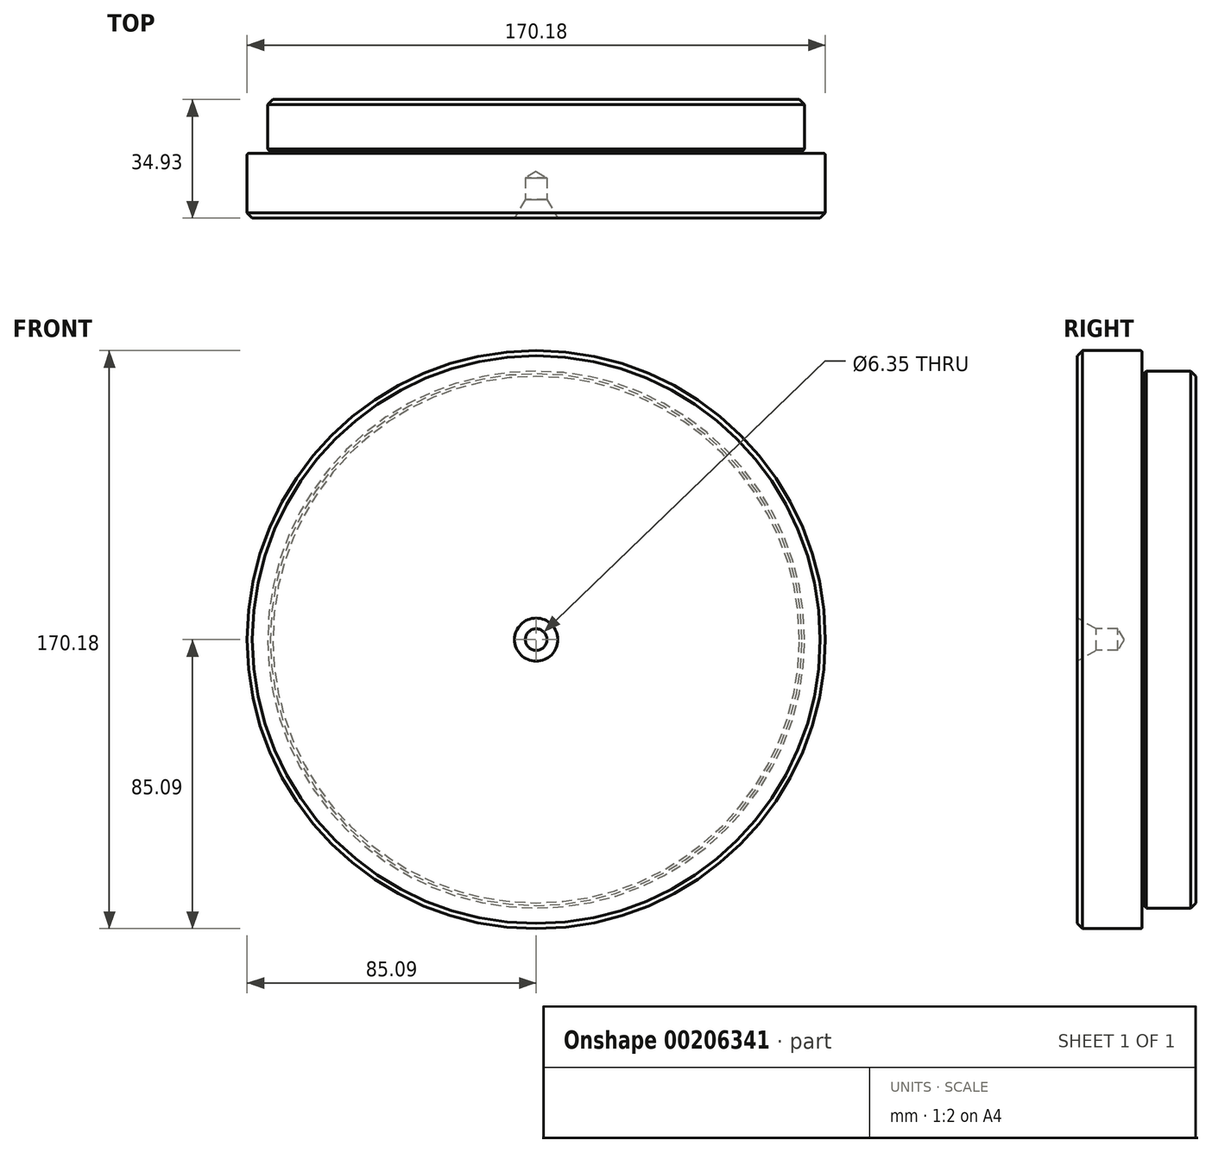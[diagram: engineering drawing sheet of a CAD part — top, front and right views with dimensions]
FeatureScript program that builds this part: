
annotation { "Feature Type Name" : "Feature", "Feature Type Description" : "" }
export const myFeature = defineFeature(function(context is Context, id is Id, definition is map)
    precondition{}
    {
        {
            var Q0;
            Q0=qCreatedBy(makeId("Right.planeOp"),FACE);
            var sketch = newSketch(context, id + "F0", { "sketchPlane" : qUnion([Q0])});
            skLineSegment(sketch, "E0", {"start": v(0, 0) * mm, "end": v(0, 79) * mm});
            skLineSegment(sketch, "E1", {"start": v(0, 79) * mm, "end": v(-14.61, 79) * mm});
            skLineSegment(sketch, "E2", {"start": v(-15.88, 79) * mm, "end": v(-15.88, 85.1) * mm});
            skLineSegment(sketch, "E3", {"start": v(-15.88, 85.1) * mm, "end": v(-34.93, 85.1) * mm});
            skLineSegment(sketch, "E4", {"start": v(-42.34, 0) * mm, "end": v(0, 0) * mm});
            skPoint(sketch, "E5", {"position": v(-15.88, 78.25) * mm});
            skLineSegment(sketch, "E6", {"start": v(-15.88, 78.25) * mm, "end": v(-15.88, 79) * mm});
            skLineSegment(sketch, "E7", {"start": v(-15.88, 78.25) * mm, "end": v(-15.37, 78.25) * mm});
            skLineSegment(sketch, "E8", {"start": v(-15.37, 78.25) * mm, "end": v(-14.61, 79) * mm});
            skLineSegment(sketch, "E9", {"start": v(-34.93, 85.1) * mm, "end": v(-34.93, 6.35) * mm});
            skLineSegment(sketch, "E10", {"start": v(-34.93, 6.35) * mm, "end": v(-29.43, 3.17) * mm});
            skLineSegment(sketch, "E11", {"start": v(-29.43, 3.18) * mm, "end": v(-23.08, 3.18) * mm});
            skLineSegment(sketch, "E12", {"start": v(-23.08, 3.18) * mm, "end": v(-21.17, 0) * mm});
            skSolve(sketch);
        }
        {
            var Q0;
            {var subQ0=sQuery(id+"F0.wireOp",EDGE,"E0");Q0=makeQuery(id+"F0.imprint","IMPRINT",FACE,{"disambiguationData":[TD([[makeQuery(id+"F0.imprint","IMPRINT",EDGE,{"derivedFrom":subQ0}),1.0]])]});}
            var Q1;
            Q1=sQuery(id+"F0.wireOp",EDGE,"E4");
            revolve(context, id + "F1", {"entities" : qUnion([Q0]), "axis" : qUnion([Q1]), "revolveType" : RevolveType.FULL});
        }
        {
            var Q0;
            Q0=makeQuery(id+"F1.opRevolve","SWEPT_EDGE",EDGE,{"disambiguationData":[OSD([sQuery(id+"F0.wireOp",EDGE,"E2"),sQuery(id+"F0.wireOp",EDGE,"E3")])]});
            fillet(context, id + "F2", {"entities" : qUnion([Q0]), "radius" : 0.5 * mm, "tangentPropagation" : true, "allowEdgeOverflow" : false});
        }
        {
            var Q0;
            Q0=makeQuery(id+"F1.opRevolve","SWEPT_EDGE",EDGE,{"disambiguationData":[OSD([sQuery(id+"F0.wireOp",EDGE,"E3"),sQuery(id+"F0.wireOp",EDGE,"Fi7OxQvJ-d1N1-gUpb-1pjk-0Ww9IjYMlTw6")])]});
            var Q1;
            Q1=makeQuery(id+"F1.opRevolve","SWEPT_EDGE",EDGE,{"disambiguationData":[OSD([sQuery(id+"F0.wireOp",EDGE,"E0"),sQuery(id+"F0.wireOp",EDGE,"E1")])]});
            chamfer(context, id + "F3", {"entities" : qUnion([Q0, Q1]), "width" : 1.52 * mm, "tangentPropagation" : true});
        }
    });
